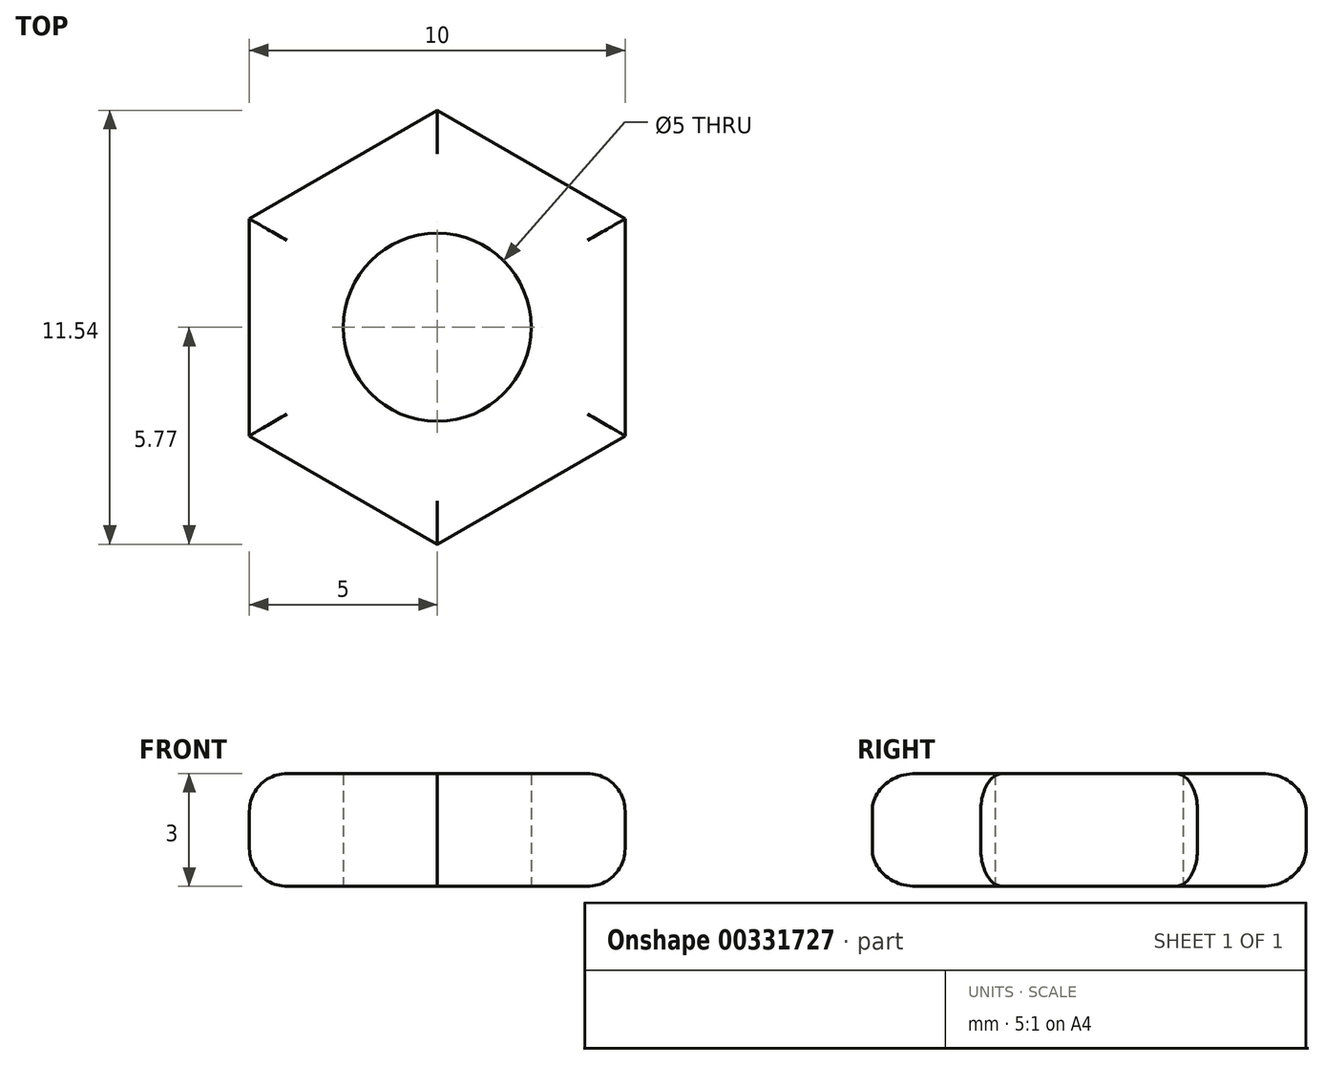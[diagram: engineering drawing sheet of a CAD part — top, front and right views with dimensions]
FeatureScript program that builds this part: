
annotation { "Feature Type Name" : "Feature", "Feature Type Description" : "" }
export const myFeature = defineFeature(function(context is Context, id is Id, definition is map)
    precondition{}
    {
        {
            var Q0;
            Q0=qCreatedBy(makeId("Top.planeOp"),FACE);
            var sketch = newSketch(context, id + "F0", { "sketchPlane" : qUnion([Q0])});
            skCircle(sketch, "E0.cCircle", {"center": v(0, 0) * mm, "radius": 5 * mm, "construction": true});
            skLineSegment(sketch, "E0.0", {"start": v(-5, -2.89) * mm, "end": v(-5, 2.89) * mm});
            skLineSegment(sketch, "E0.1", {"start": v(-5, 2.89) * mm, "end": v(0, 5.77) * mm});
            skLineSegment(sketch, "E0.2", {"start": v(0, 5.77) * mm, "end": v(5, 2.89) * mm});
            skLineSegment(sketch, "E0.3", {"start": v(5, 2.89) * mm, "end": v(5, -2.89) * mm});
            skLineSegment(sketch, "E0.4", {"start": v(5, -2.89) * mm, "end": v(0, -5.77) * mm});
            skLineSegment(sketch, "E0.5", {"start": v(0, -5.77) * mm, "end": v(-5, -2.89) * mm});
            skPoint(sketch, "E0.0.midPoint", {"position": v(-5, 0) * mm});
            skCircle(sketch, "E1", {"center": v(0, 0) * mm, "radius": 2.5 * mm});
            skSolve(sketch);
        }
        {
            var Q0;
            Q0 = qSketchRegion(id + "F0", true);
            extrude(context, id + "F1", {"entities" : qUnion([Q0]), "depth" : 3 * mm});
        }
        {
            var Q0;
            Q0=makeQuery(id+"F1.opExtrude","CAP_EDGE",EDGE,{"disambiguationData":[OSD([sQuery(id+"F0.wireOp",EDGE,"E0.3")])],"isStart":true});
            var Q1;
            Q1=makeQuery(id+"F1.opExtrude","CAP_EDGE",EDGE,{"disambiguationData":[OSD([sQuery(id+"F0.wireOp",EDGE,"E0.2")])],"isStart":true});
            var Q2;
            Q2=makeQuery(id+"F1.opExtrude","CAP_EDGE",EDGE,{"disambiguationData":[OSD([sQuery(id+"F0.wireOp",EDGE,"E0.1")])],"isStart":true});
            var Q3;
            Q3=makeQuery(id+"F1.opExtrude","CAP_EDGE",EDGE,{"disambiguationData":[OSD([sQuery(id+"F0.wireOp",EDGE,"E0.0")])],"isStart":true});
            var Q4;
            Q4=makeQuery(id+"F1.opExtrude","CAP_EDGE",EDGE,{"disambiguationData":[OSD([sQuery(id+"F0.wireOp",EDGE,"E0.5")])],"isStart":true});
            var Q5;
            Q5=makeQuery(id+"F1.opExtrude","CAP_EDGE",EDGE,{"disambiguationData":[OSD([sQuery(id+"F0.wireOp",EDGE,"E0.4")])],"isStart":true});
            var Q6;
            Q6=makeQuery(id+"F1.opExtrude","CAP_EDGE",EDGE,{"disambiguationData":[OSD([sQuery(id+"F0.wireOp",EDGE,"E0.3")])],"isStart":false});
            var Q7;
            Q7=makeQuery(id+"F1.opExtrude","CAP_EDGE",EDGE,{"disambiguationData":[OSD([sQuery(id+"F0.wireOp",EDGE,"E0.4")])],"isStart":false});
            var Q8;
            Q8=makeQuery(id+"F1.opExtrude","CAP_EDGE",EDGE,{"disambiguationData":[OSD([sQuery(id+"F0.wireOp",EDGE,"E0.5")])],"isStart":false});
            var Q9;
            Q9=makeQuery(id+"F1.opExtrude","CAP_EDGE",EDGE,{"disambiguationData":[OSD([sQuery(id+"F0.wireOp",EDGE,"E0.0")])],"isStart":false});
            var Q10;
            Q10=makeQuery(id+"F1.opExtrude","CAP_EDGE",EDGE,{"disambiguationData":[OSD([sQuery(id+"F0.wireOp",EDGE,"E0.1")])],"isStart":false});
            var Q11;
            Q11=makeQuery(id+"F1.opExtrude","CAP_EDGE",EDGE,{"disambiguationData":[OSD([sQuery(id+"F0.wireOp",EDGE,"E0.2")])],"isStart":false});
            fillet(context, id + "F2", {"entities" : qUnion([Q0, Q1, Q2, Q3, Q4, Q5, Q6, Q7, Q8, Q9, Q10, Q11]), "radius" : 1 * mm, "tangentPropagation" : true, "allowEdgeOverflow" : false});
        }
    });
